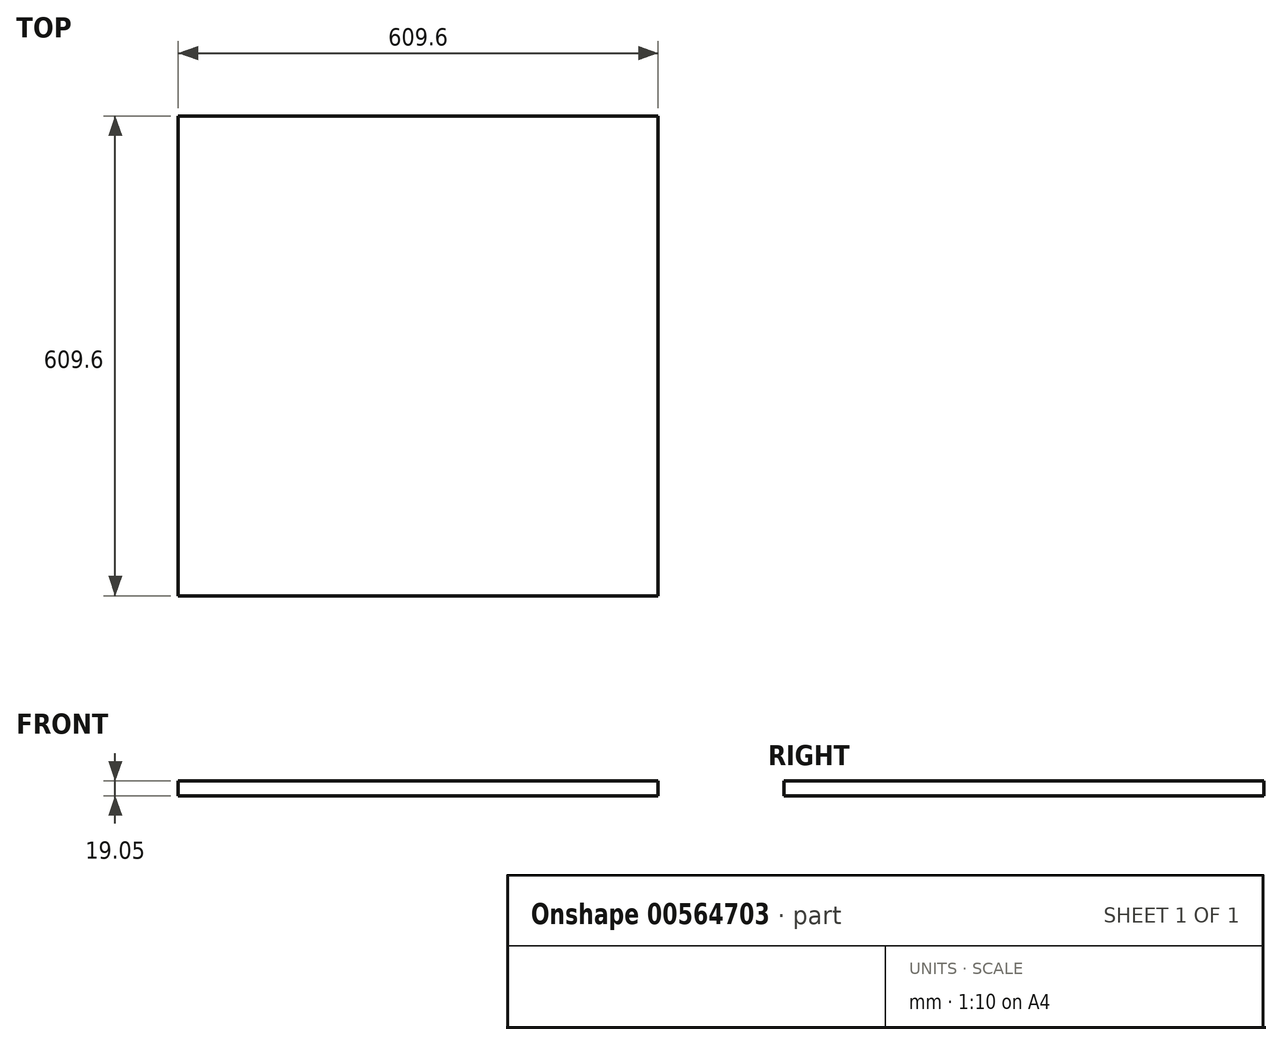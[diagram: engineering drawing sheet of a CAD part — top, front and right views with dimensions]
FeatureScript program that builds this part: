
annotation { "Feature Type Name" : "Feature", "Feature Type Description" : "" }
export const myFeature = defineFeature(function(context is Context, id is Id, definition is map)
    precondition{}
    {
        {
            var Q0;
            Q0=qCreatedBy(makeId("Top.planeOp"),FACE);
            var sketch = newSketch(context, id + "F0", { "sketchPlane" : qUnion([Q0])});
            skLineSegment(sketch, "E0.bottom", {"start": v(304.8, 304.8) * mm, "end": v(-304.8, 304.8) * mm});
            skLineSegment(sketch, "E0.top", {"start": v(304.8, -304.8) * mm, "end": v(-304.8, -304.8) * mm});
            skLineSegment(sketch, "E0.left", {"start": v(304.8, 304.8) * mm, "end": v(304.8, -304.8) * mm});
            skLineSegment(sketch, "E0.right", {"start": v(-304.8, 304.8) * mm, "end": v(-304.8, -304.8) * mm});
            skPoint(sketch, "E0.middle", {"position": v(0, 0) * mm});
            skSolve(sketch);
        }
        {
            var Q0;
            Q0=makeQuery(id+"F0.imprint","IMPRINT",FACE,{"disambiguationData":[TD([[makeQuery(id+"F0.imprint","IMPRINT",EDGE,{"derivedFrom":sQuery(id+"F0.wireOp",EDGE,"E0.bottom")}),1.0]])]});
            extrude(context, id + "F1", {"entities" : qUnion([Q0]), "depth" : 19.05 * mm, "offsetDistance" : 25.4 * mm});
        }
    });
